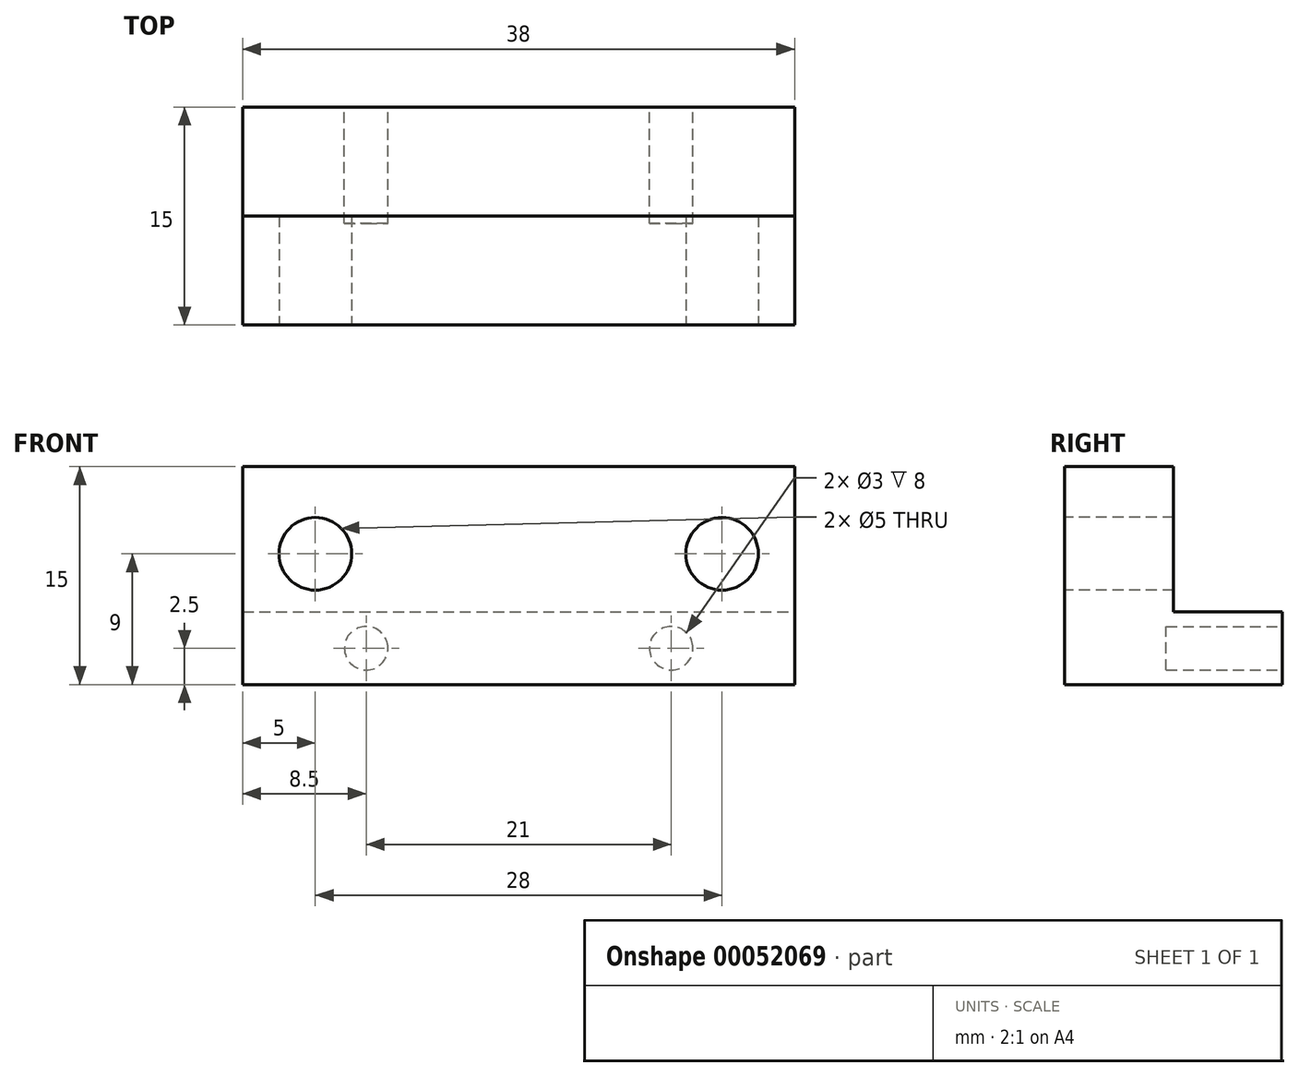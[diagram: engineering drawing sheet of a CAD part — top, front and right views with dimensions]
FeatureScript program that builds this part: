
annotation { "Feature Type Name" : "Feature", "Feature Type Description" : "" }
export const myFeature = defineFeature(function(context is Context, id is Id, definition is map)
    precondition{}
    {
        {
            var Q0;
            Q0=qCreatedBy(makeId("Front.planeOp"),FACE);
            var sketch = newSketch(context, id + "F0", { "sketchPlane" : qUnion([Q0])});
            skLineSegment(sketch, "E0.rect.bottom", {"start": v(19, -2.5) * mm, "end": v(-19, -2.5) * mm});
            skLineSegment(sketch, "E0.rect.top", {"start": v(19, 2.5) * mm, "end": v(-19, 2.5) * mm});
            skLineSegment(sketch, "E0.rect.left", {"start": v(19, -2.5) * mm, "end": v(19, 2.5) * mm});
            skLineSegment(sketch, "E0.rect.right", {"start": v(-19, -2.5) * mm, "end": v(-19, 2.5) * mm});
            skPoint(sketch, "E0.rect.middle", {"position": v(0, 0) * mm});
            skSolve(sketch);
        }
        {
            var Q0;
            Q0=makeQuery(id+"F0.imprint","IMPRINT",FACE,{"disambiguationData":[TD([[makeQuery(id+"F0.imprint","IMPRINT",EDGE,{"derivedFrom":sQuery(id+"F0.wireOp",EDGE,"E0.rect.bottom")}),-1.0]])]});
            extrude(context, id + "F1", {"entities" : qUnion([Q0]), "depth" : 15 * mm});
        }
        {
            var Q0;
            Q0=makeQuery(id+"F0.imprint","IMPRINT",FACE,{"disambiguationData":[TD([[makeQuery(id+"F0.imprint","IMPRINT",EDGE,{"derivedFrom":sQuery(id+"F0.wireOp",EDGE,"E0.rect.bottom")}),-1.0]])]});
            var sketch = newSketch(context, id + "F2", { "sketchPlane" : qUnion([Q0])});
            skCircle(sketch, "E1", {"center": v(-10.5, 0) * mm, "radius": 1.5 * mm});
            skCircle(sketch, "E2", {"center": v(10.5, 0) * mm, "radius": 1.5 * mm});
            skSolve(sketch);
        }
        {
            var Q0;
            Q0 = qSketchRegion(id + "F2", true);
            var Q1;
            Q1=makeQuery(id+"F2.imprint","IMPRINT",FACE,{"disambiguationData":[TD([[makeQuery(id+"F2.imprint","IMPRINT",EDGE,{"derivedFrom":sQuery(id+"F2.wireOp",EDGE,"E1")}),1.0]])]});
            var Q2;
            Q2=makeQuery(id+"F2.imprint","IMPRINT",FACE,{"disambiguationData":[TD([[makeQuery(id+"F2.imprint","IMPRINT",EDGE,{"derivedFrom":sQuery(id+"F2.wireOp",EDGE,"E2")}),1.0]])]});
            extrude(context, id + "F3", {"entities" : qUnion([Q0, Q1, Q2]), "operationType" : NewBodyOperationType.REMOVE, "depth" : 8 * mm});
        }
        {
            var Q0;
            Q0=makeQuery(id+"F1.opExtrude","SWEPT_FACE",FACE,{"disambiguationData":[OSD([sQuery(id+"F0.wireOp",EDGE,"E0.rect.top")])]});
            var sketch = newSketch(context, id + "F4", { "sketchPlane" : qUnion([Q0])});
            skLineSegment(sketch, "E3.bottom", {"start": v(-19, -15) * mm, "end": v(19, -15) * mm});
            skLineSegment(sketch, "E3.top", {"start": v(-19, -7.5) * mm, "end": v(19, -7.5) * mm});
            skLineSegment(sketch, "E3.left", {"start": v(-19, -15) * mm, "end": v(-19, -7.5) * mm});
            skLineSegment(sketch, "E3.right", {"start": v(19, -15) * mm, "end": v(19, -7.5) * mm});
            skSolve(sketch);
        }
        {
            var Q0;
            Q0 = qSketchRegion(id + "F4", true);
            extrude(context, id + "F5", {"entities" : qUnion([Q0]), "operationType" : NewBodyOperationType.ADD, "depth" : 10 * mm});
        }
        {
            var Q0;
            Q0=makeQuery(id+"F5.boolean.opBoolean","MERGE",FACE,{"derivedFrom":[makeQuery(id+"F1.opExtrude","CAP_FACE",FACE,{"disambiguationData":[OSD([sQuery(id+"F0.wireOp",EDGE,"E0.rect.bottom"),sQuery(id+"F0.wireOp",EDGE,"E0.rect.top"),sQuery(id+"F0.wireOp",EDGE,"E0.rect.left"),sQuery(id+"F0.wireOp",EDGE,"E0.rect.right")])],"isStart":false}),makeQuery(id+"F5.opExtrude","SWEPT_FACE",FACE,{"disambiguationData":[OSD([sQuery(id+"F4.wireOp",EDGE,"E3.bottom")])]})]});
            var sketch = newSketch(context, id + "F6", { "sketchPlane" : qUnion([Q0])});
            skCircle(sketch, "E4", {"center": v(-14, 6.5) * mm, "radius": 2.5 * mm});
            skCircle(sketch, "E5", {"center": v(14, 6.5) * mm, "radius": 2.5 * mm});
            skSolve(sketch);
        }
        {
            var Q0;
            Q0 = qSketchRegion(id + "F6", true);
            extrude(context, id + "F7", {"entities" : qUnion([Q0]), "operationType" : NewBodyOperationType.REMOVE, "oppositeDirection" : true, "depth" : 10 * mm});
        }
    });
